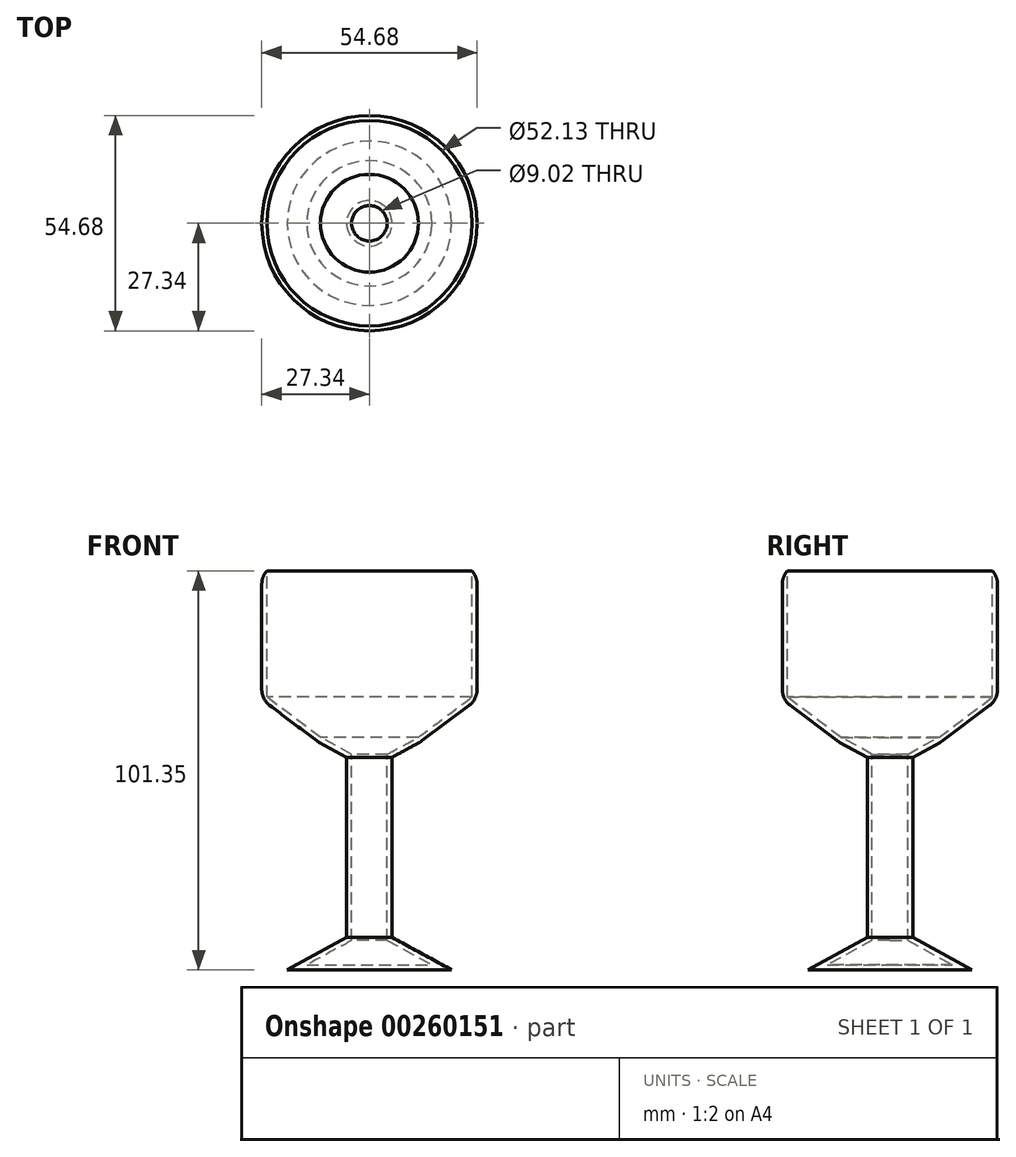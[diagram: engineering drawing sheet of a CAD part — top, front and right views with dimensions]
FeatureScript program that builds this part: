
annotation { "Feature Type Name" : "Feature", "Feature Type Description" : "" }
export const myFeature = defineFeature(function(context is Context, id is Id, definition is map)
    precondition{}
    {
        {
            var Q0;
            Q0=qCreatedBy(makeId("Front.planeOp"),FACE);
            var sketch = newSketch(context, id + "F0", { "sketchPlane" : qUnion([Q0])});
            skLineSegment(sketch, "E0", {"start": v(0, 47.34) * mm, "end": v(-27.34, 47.34) * mm});
            skLineSegment(sketch, "E1", {"start": v(-27.34, 47.34) * mm, "end": v(-27.34, 14.67) * mm});
            skLineSegment(sketch, "E2", {"start": v(-27.34, 14.67) * mm, "end": v(-13.11, 4) * mm});
            skLineSegment(sketch, "E3", {"start": v(-13.11, 4) * mm, "end": v(-5.78, 0) * mm});
            skLineSegment(sketch, "E4", {"start": v(-5.78, 0) * mm, "end": v(-5.78, -45.78) * mm});
            skLineSegment(sketch, "E5", {"start": v(-5.78, -45.78) * mm, "end": v(-20.9, -54) * mm});
            skLineSegment(sketch, "E6", {"start": v(-20.9, -54) * mm, "end": v(0, -54) * mm});
            skLineSegment(sketch, "E7", {"start": v(0, 47.34) * mm, "end": v(0, -54) * mm});
            skSolve(sketch);
        }
        {
            var Q0;
            Q0 = qSketchRegion(id + "F0", true);
            var Q1;
            Q1=sQuery(id+"F0.wireOp",EDGE,"E7");
            revolve(context, id + "F1", {"entities" : qUnion([Q0]), "axis" : qUnion([Q1]), "revolveType" : RevolveType.FULL});
        }
        {
            var Q0;
            Q0=makeQuery(id+"F1.opRevolve","SWEPT_FACE",FACE,{"disambiguationData":[OSD([sQuery(id+"F0.wireOp",EDGE,"E0")])]});
            shell(context, id + "F2", {"entities" : qUnion([Q0]), "thickness" : 1.27 * mm});
        }
        {
            var Q0;
            Q0=makeQuery(id+"F1.opRevolve","SWEPT_EDGE",EDGE,{"disambiguationData":[OSD([sQuery(id+"F0.wireOp",EDGE,"E0"),sQuery(id+"F0.wireOp",EDGE,"E1")])]});
            fillet(context, id + "F3", {"entities" : qUnion([Q0]), "radius" : 5.08 * mm, "tangentPropagation" : true, "allowEdgeOverflow" : false});
        }
        {
            var Q0;
            Q0=makeQuery(id+"F1.opRevolve","SWEPT_FACE",FACE,{"disambiguationData":[OSD([sQuery(id+"F0.wireOp",EDGE,"E2")])]});
            fillet(context, id + "F4", {"entities" : qUnion([Q0]), "radius" : 5.08 * mm, "tangentPropagation" : true, "allowEdgeOverflow" : false});
        }
    });
